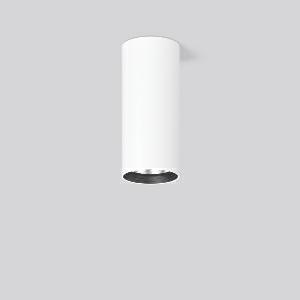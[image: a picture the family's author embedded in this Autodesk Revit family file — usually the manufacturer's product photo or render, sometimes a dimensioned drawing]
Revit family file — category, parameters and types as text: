
# Revit family: heledon_mini_a_931201_002_1_3a6d
name_source: partatom
category: Lighting Fixtures
units: mm (PartAtom-declared; Revit-internal decimal feet)

## family parameters
Cut with Voids When Loaded = No
Host = Face
Light Source = No
Part Type = Normal
Room Calculation Point = No
Round Connector Dimension = Use Diameter
Shared = No

## types (1)
- HELEDON mini A (1 x LED Modul 940, 2600 lm, 4000)
    Apparent Load = 20 VA
    Approval mark = CE
    CIE Flux Codes = 99 100 100 100 100
    Color Rendering = 92
    Color Temperature = 4000
    Default Elevation = 1800 mm
    Description = Series: HELEDON mini
Cylindrical surface-mounted downlight. Housing: die-cast aluminium, powder-coated. Internal ceiling frame polycarbonate with bayonet mounting. Black plastic ring and recessed LED to prevent glare from the side. Optical assembly with reflector made of MIRO-Silver with 98% total light reflection for outstanding efficiency - can be changed without tools. Best colour rendering index Ra>90. Suitable for Ceiling mounting. Easy installation with a separate ceiling frame with bayonet mounting and plug connection. Driver integrated. Connected via plug-in connector. High quality converter without flickering and stroboscopic effect. The following accessories can be mounted without use of tools: interchangeable lenses, decorative glasses, honeycomb louvre, clear and frosted diffusers, white interchangeable plastic ring. 
Colour: traffic white, matt (RAL 9016)
Diameter: 87 mm
Height: 197 mm
Lamp: LED
Socket: without socket
Colour temperature: 4000K
Colour rendering index (CRI): 92
System power: 20 W
Rated luminous flux: 2600 lm
Luminous efficiency: 130 lm/W
Control gear: Regulated power supply
Protection class: I
Type of protection: IP 20
    Height = 197 mm
    Lamp = 1 x LED Modul 940
    Lamp Light Flux = 2600 lm
    Lamp count = 1
    Length = 87 mm
    Lifetime = 50000 h
    Luminous efficacy = 130 lm/W
    Manufacturer = RZB
    ModVariant = No
    Model = 931201.002.1
    Mounting Place = Ceiling
    Mounting Type = Surface mounted
    Number of Poles = 1
    OnlyDefault = Yes
    Power Factor = 1
    Product Name = HELEDON mini A
    Product group = Surface mounted downlights
    ProductGroupID = 302
    Protection Class = Protection class I
    Protection Degree = IP 20
    RLX_Detail_Level = 1
    RLX_Emergency_Light_Flux = 0 lm
    RLX_Emergency_Type = 0
    RLX_Emergency_Type_DB = No
    RlxData = <blob elided: 106653 chars, md5=a1ddd99e>
    Socket = socket
    Standby Power = 0 W
    System Light Flux = 2600 lm
    System Power = 20 W
    Type Comments = Product without accessories
    Type Image = 931188.002.jpg
    URL = http://relux.com
    VarID = ---
    Voltage = 230 V
    Voltage Range = 220-240 V
    Weight = 0.00 kg
    Width = 0 mm  [stored 0 ft]

note: [stored X ft] marks values corroborated as IEEE doubles in the binary element streams (Revit-internal decimal feet)

## geometry (parser evidence)
native form markers: Blend x4, Sweep x9
no freeform markers — native parametric forms only
